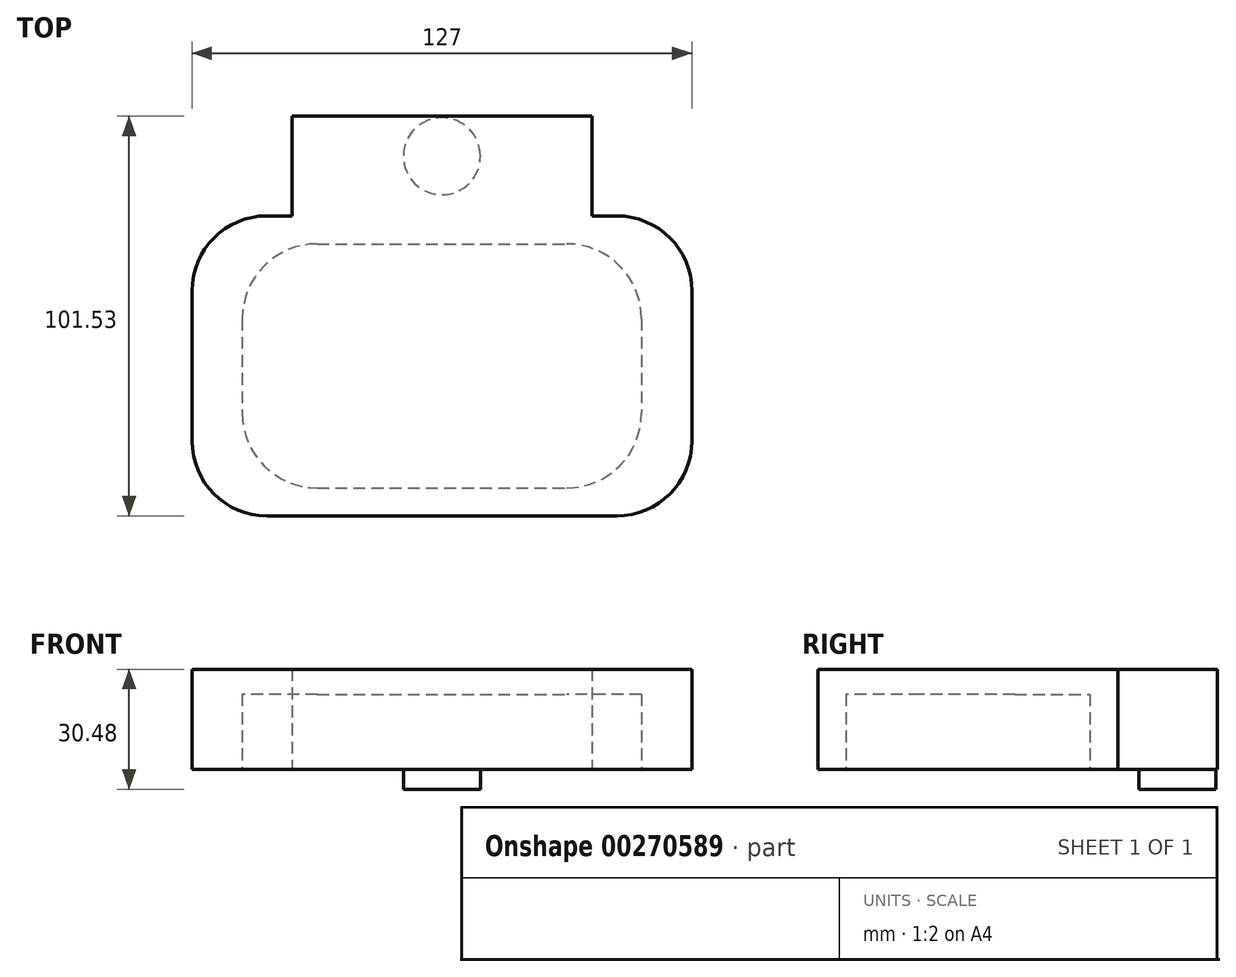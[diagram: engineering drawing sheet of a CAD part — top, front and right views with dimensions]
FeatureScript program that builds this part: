
annotation { "Feature Type Name" : "Feature", "Feature Type Description" : "" }
export const myFeature = defineFeature(function(context is Context, id is Id, definition is map)
    precondition{}
    {
        {
            var Q0;
            Q0=qCreatedBy(makeId("Top.planeOp"),FACE);
            var sketch = newSketch(context, id + "F0", { "sketchPlane" : qUnion([Q0])});
            skLineSegment(sketch, "E0.bottom", {"start": v(-44.45, -38.1) * mm, "end": v(44.45, -38.1) * mm});
            skLineSegment(sketch, "E0.top", {"start": v(-44.45, 38.1) * mm, "end": v(44.45, 38.1) * mm});
            skLineSegment(sketch, "E0.left", {"start": v(-63.5, -19.05) * mm, "end": v(-63.5, 19.05) * mm});
            skLineSegment(sketch, "E0.right", {"start": v(63.5, -19.05) * mm, "end": v(63.5, 19.05) * mm});
            skPoint(sketch, "E0.middle", {"position": v(0, 0) * mm});
            skPoint(sketch, "E1.visualSharp", {"position": v(63.5, -38.1) * mm});
            skArc(sketch, "E1.filletArc", {"start": v(44.45, -38.1) * mm, "mid": v(57.92, -32.52) * mm, "end": v(63.5, -19.05) * mm});
            skPoint(sketch, "E2.visualSharp", {"position": v(-63.5, -38.1) * mm});
            skArc(sketch, "E2.filletArc", {"start": v(-63.5, -19.05) * mm, "mid": v(-57.92, -32.52) * mm, "end": v(-44.45, -38.1) * mm});
            skPoint(sketch, "E3.visualSharp", {"position": v(63.5, 38.1) * mm});
            skArc(sketch, "E3.filletArc", {"start": v(63.5, 19.05) * mm, "mid": v(57.92, 32.52) * mm, "end": v(44.45, 38.1) * mm});
            skPoint(sketch, "E4.visualSharp", {"position": v(-63.5, 38.1) * mm});
            skArc(sketch, "E4.filletArc", {"start": v(-44.45, 38.1) * mm, "mid": v(-57.92, 32.52) * mm, "end": v(-63.5, 19.05) * mm});
            skLineSegment(sketch, "E5", {"start": v(-38.1, 38.1) * mm, "end": v(-38.1, 63.43) * mm});
            skLineSegment(sketch, "E6", {"start": v(-38.1, 63.43) * mm, "end": v(38.1, 63.43) * mm});
            skLineSegment(sketch, "E7", {"start": v(38.1, 63.43) * mm, "end": v(38.1, 38.1) * mm});
            skLineSegment(sketch, "E8.bottom", {"start": v(-31.67, 31) * mm, "end": v(31.67, 31) * mm});
            skLineSegment(sketch, "E8.top", {"start": v(-31.67, -31) * mm, "end": v(31.67, -31) * mm});
            skLineSegment(sketch, "E8.left", {"start": v(-50.72, 11.95) * mm, "end": v(-50.72, -11.95) * mm});
            skLineSegment(sketch, "E8.right", {"start": v(50.72, 11.95) * mm, "end": v(50.72, -11.95) * mm});
            skPoint(sketch, "E9.visualSharp", {"position": v(-50.72, 31) * mm});
            skArc(sketch, "E9.filletArc", {"start": v(-31.67, 31) * mm, "mid": v(-45.14, 25.42) * mm, "end": v(-50.72, 11.95) * mm});
            skPoint(sketch, "E10.visualSharp", {"position": v(50.72, 31) * mm});
            skArc(sketch, "E10.filletArc", {"start": v(50.72, 11.95) * mm, "mid": v(45.14, 25.42) * mm, "end": v(31.67, 31) * mm});
            skPoint(sketch, "E11.visualSharp", {"position": v(50.72, -31) * mm});
            skArc(sketch, "E11.filletArc", {"start": v(31.67, -31) * mm, "mid": v(45.14, -25.42) * mm, "end": v(50.72, -11.95) * mm});
            skPoint(sketch, "E12.visualSharp", {"position": v(-50.72, -31) * mm});
            skArc(sketch, "E12.filletArc", {"start": v(-50.72, -11.95) * mm, "mid": v(-45.14, -25.42) * mm, "end": v(-31.67, -31) * mm});
            skSolve(sketch);
        }
        {
            var Q0;
            Q0=makeQuery(id+"F0.imprint","IMPRINT",FACE,{"disambiguationData":[TD([[makeQuery(id+"F0.imprint","IMPRINT",EDGE,{"derivedFrom":sQuery(id+"F0.wireOp",EDGE,"E8.bottom")}),-1.0]])]});
            var Q1;
            Q1=makeQuery(id+"F0.imprint","IMPRINT",FACE,{"disambiguationData":[TD([[makeQuery(id+"F0.imprint","IMPRINT",EDGE,{"derivedFrom":sQuery(id+"F0.wireOp",EDGE,"E0.bottom")}),1.0]])]});
            var Q2;
            {var subQ0=sQuery(id+"F0.wireOp",EDGE,"E5");Q2=makeQuery(id+"F0.imprint","IMPRINT",FACE,{"disambiguationData":[TD([[makeQuery(id+"F0.imprint","IMPRINT",EDGE,{"derivedFrom":subQ0}),-1.0]])]});}
            extrude(context, id + "F1", {"entities" : qUnion([Q0, Q1, Q2]), "depth" : 25.4 * mm});
        }
        {
            var Q0;
            Q0=makeQuery(id+"F0.imprint","IMPRINT",FACE,{"disambiguationData":[TD([[makeQuery(id+"F0.imprint","IMPRINT",EDGE,{"derivedFrom":sQuery(id+"F0.wireOp",EDGE,"E8.bottom")}),-1.0]])]});
            extrude(context, id + "F2", {"entities" : qUnion([Q0]), "operationType" : NewBodyOperationType.REMOVE, "depth" : 19.05 * mm});
        }
        {
            var Q0;
            Q0=makeQuery(id+"F1.opExtrude","CAP_FACE",FACE,{"disambiguationData":[OSD([sQuery(id+"F0.wireOp",EDGE,"E0.bottom"),sQuery(id+"F0.wireOp",EDGE,"E0.top"),sQuery(id+"F0.wireOp",EDGE,"E0.left"),sQuery(id+"F0.wireOp",EDGE,"E0.right"),sQuery(id+"F0.wireOp",EDGE,"E1.filletArc"),sQuery(id+"F0.wireOp",EDGE,"E2.filletArc"),sQuery(id+"F0.wireOp",EDGE,"E3.filletArc"),sQuery(id+"F0.wireOp",EDGE,"E4.filletArc"),sQuery(id+"F0.wireOp",EDGE,"E5"),sQuery(id+"F0.wireOp",EDGE,"E6"),sQuery(id+"F0.wireOp",EDGE,"E7")])],"isStart":true});
            var sketch = newSketch(context, id + "F3", { "sketchPlane" : qUnion([Q0])});
            skCircle(sketch, "E13", {"center": v(0, -53.28) * mm, "radius": 9.77 * mm});
            skSolve(sketch);
        }
        {
            var Q0;
            Q0=makeQuery(id+"F3.imprint","IMPRINT",FACE,{"disambiguationData":[TD([[makeQuery(id+"F3.imprint","IMPRINT",EDGE,{"derivedFrom":sQuery(id+"F3.wireOp",EDGE,"E13")}),1.0]])]});
            extrude(context, id + "F4", {"entities" : qUnion([Q0]), "operationType" : NewBodyOperationType.ADD, "depth" : 5.08 * mm});
        }
    });
